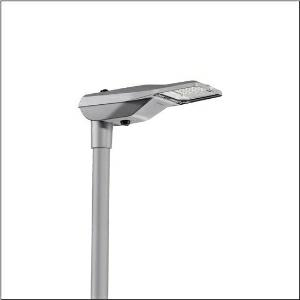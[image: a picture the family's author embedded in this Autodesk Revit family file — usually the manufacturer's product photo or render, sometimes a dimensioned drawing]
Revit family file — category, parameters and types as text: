
# Revit family: streetlight_sl_21_micro___p0_8ab_5xe1r33t08db_81a7
name_source: partatom
category: Lighting Fixtures
units: mm (PartAtom-declared; Revit-internal decimal feet)

## family parameters
Cut with Voids When Loaded = No
Host = Face
Light Source = No
Part Type = Normal
Room Calculation Point = No
Round Connector Dimension = Use Diameter
Shared = No

## types (1)
- --- (1 x LED, 4470 lm, 39.1 W, 3000K)
    Apparent Load = 39 VA
    CIE Flux Codes = 36 71 98 100 100
    Color Rendering = 70
    Color Temperature = 3000K
    Default Elevation = 1800 mm
    Description = Streetlight SL 21 micro, mast luminaire, primary light control with lens, of PMMA, primary optical cover: cover, of toughened safety glass, transparent, light distribution: P0.8aB, light emission: direct distribution, primary light characteristic: asymmetric, installation type: post-top, side-entry, LED, High Power LED, rated luminous flux: 4.470lm, luminous efficacy: 114lm/W, light colour: 730, colour temperature: 3000K, control gear: D4i, control: pre-setting: logarithmic dimming characteristic, flexible luminous flux parameterisation, time-dependent luminous flux control, constant luminous flux control, overheat protection, mains connection: 220..240V, AC, 50/60Hz, start of lifetime: 39W, end of service life: 41W, reduction: 18W, luminaire housing, of diecast aluminium, powder-coated, SITECO metallic grey (DB 702S), corrosivity category C5 high according to DIN EN ISO 12944, multi-level sealing system, sealing non-destructively replaceable, inclination adjustable: 0°, 5°, 10°, 15°, please order mast flange separately, length: 528mm, width: 235mm, height: 110mm, mast flange for spigot size: 42mm (side-entry): 5XC10008XM4, 60/48mm (side-entry/post-top): 5XC10108XM2, 76/60mm (side-entry/post-top): 5XC10108XM1, Smart Interface below and above, protection rating (complete): IP66, insulation class (complete): insulation class II (safety insulation), certification: CE, ENEC, ENEC+, VDE, impact resistance: IK10, permissible operating ambient temperature for outdoor applications: -40..+50°C, standard-compliant lighting for roads and squares, packaging unit: 1 piece

Light Distribution: P0.8aB
    Height = 110 mm
    Lamp = 1 x LED
    Lamp Light Flux = 4470 lm
    Lamp Power = 39.1 W
    Lamp count = 1
    Length = 528 mm
    Luminous efficacy = 114 lm/W
    Manufacturer = Siteco
    ModVariant = No
    Model = 5XE1R33T08DB
    Number of Poles = 1
    OnlyDefault = Yes
    Power Factor = 1
    Product Name = Streetlight SL 21 micro | P0.8aB
    Product group = mast luminaire | pylon top
    ProductGroupID = 6100
    Protection Class = Protection class II
    Protection Degree = IP 66
    RLX_Detail_Level = 1
    RLX_Emergency_Light_Flux = 0 lm
    RLX_Emergency_Type = 0
    RLX_Emergency_Type_DB = No
    RlxData = <blob elided: 98625 chars, md5=98fc61f6>
    Socket = socket
    Standby Power = 0 W
    System Light Flux = 4470 lm
    System Power = 39 W
    Type Comments = factory setting: luminous flux: 100 % | dim-lin: 254 | 765 mA
    Type Image = l_1007239.jpg
    URL = http://relux.com
    VarID = @adj_082823
    Voltage = 0 V
    Weight = 0.00 kg
    Width = 235 mm

## geometry (parser evidence)
native form markers: Blend x4, Sweep x10
no freeform markers — native parametric forms only
